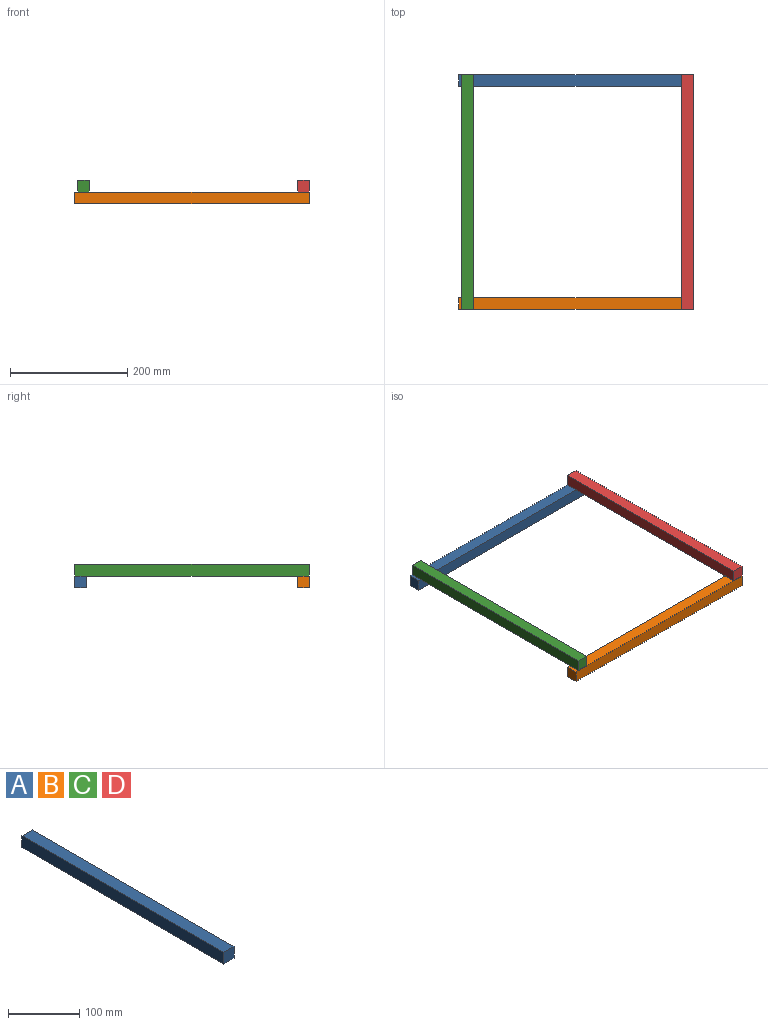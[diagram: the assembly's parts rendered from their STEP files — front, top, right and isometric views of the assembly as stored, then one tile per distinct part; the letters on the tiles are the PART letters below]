
ASSEMBLY  parts=4 mates=3
PART A: 6 faces, bbox 20x400x20 mm
  f0: plane 400x20mm, normal (0,0,-1), area 8000mm2, adj f1,f3,f4,f5
  f1: plane 400x20mm, normal (1,0,0), area 8000mm2, adj f0,f2,f4,f5
  f2: plane 400x20mm, normal (0,0,1), area 8000mm2, adj f1,f3,f4,f5
  f3: plane 400x20mm, normal (-1,0,0), area 8000mm2, adj f0,f2,f4,f5
  f4: plane 20x20mm, normal (0,-1,0), area 400mm2, adj f0,f1,f2,f3
  f5: plane 20x20mm, normal (0,1,0), area 400mm2, adj f0,f1,f2,f3
PART B: same geometry as A
PART C: same geometry as A
PART D: same geometry as A
PLACE A rot(axis=(0,0,-1),90deg) t=(-190,190,-20)mm
PLACE B rot(axis=(0.58,0.58,-0.58),120deg) t=(-190,-190,-20)mm
PLACE C t=(-374.94,0,0)mm
PLACE D at identity fixed
MATE fastened D.f1 <-> B.f5  axis (1,0,0) through (10,-200,-10)mm
MATE fastened A.f5 <-> D.f1  axis (1,0,0) through (10,200,-10)mm
MATE slider D.f3 <-> C.f1  axis (-1,0,0) through (-10,0,0)mm
